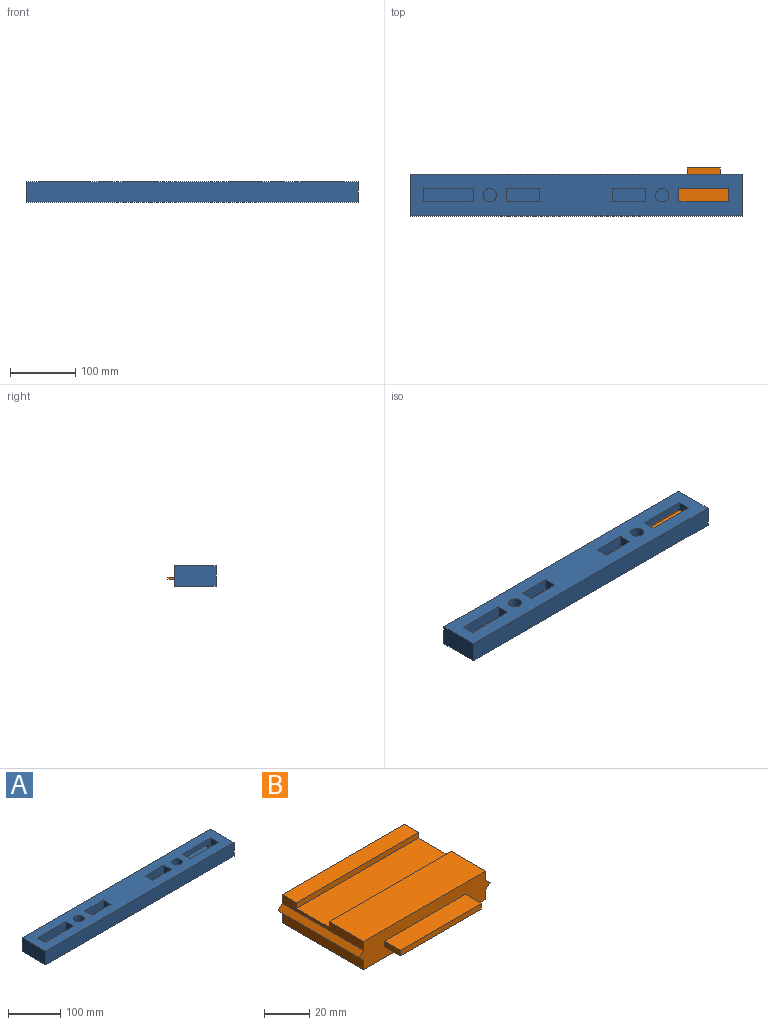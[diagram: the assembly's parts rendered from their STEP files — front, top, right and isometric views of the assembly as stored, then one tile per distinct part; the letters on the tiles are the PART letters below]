
ASSEMBLY  parts=2 mates=1
PART A: 39 faces, bbox 508x63.5x31.8 mm
  f0: plane 508x31.75mm, normal (0,1,0), area 14953.2mm2, adj f3,f4,f6,f7,f13,f14,f29,f30
  f1: plane 76.2x11.43mm, normal (0,-1,0), area 871mm2, adj f3,f13,f14,f29
  f2: plane 76.2x11.43mm, normal (0,1,0), area 871mm2, adj f3,f13,f14,f35
  f3: plane 508x63.5mm, normal (0,0,1), area 26448.1mm2, adj f0,f1,f2,f4,f5,f6,f8,f9
  f4: plane 63.5x31.75mm, normal (-1,0,0), area 2016.1mm2, adj f0,f3,f5,f7
  f5: plane 508x31.75mm, normal (0,-1,0), area 16129mm2, adj f3,f4,f6,f7
  f6: plane 63.5x31.75mm, normal (1,0,0), area 2016.1mm2, adj f0,f3,f5,f7
  f7: plane 508x63.5mm, normal (0,0,-1), area 32258mm2, adj f0,f4,f5,f6
  f8: plane 50.8x18mm, normal (0,-1,0), area 914.4mm2, adj f3,f9,f11,f12
  f9: plane 20.32x18mm, normal (1,0,0), area 365.8mm2, adj f3,f8,f10,f12
  f10: plane 50.8x18mm, normal (0,1,0), area 914.4mm2, adj f3,f9,f11,f12
  f11: plane 20.32x18mm, normal (-1,0,0), area 365.8mm2, adj f3,f8,f10,f12
  f12: plane 50.8x20.32mm, normal (0,0,1), area 1032.3mm2, adj f8,f9,f10,f11
  f13: plane 50.8x16.2mm, normal (1,0,0), area 474.7mm2, adj f0,f1,f2,f3,f29,f34,f35,f38
  f14: plane 50.8x16.2mm, normal (-1,0,0), area 474.7mm2, adj f0,f1,f2,f3,f29,f35,f36,f38
  f15: cylinder r=10.16mm len=20.32mm, axis (0,0,1), area 1149.1mm2, adj f3,f16
  f16: plane 20.32x20.32mm, normal (0,0,1), area 324.3mm2, adj f15
  f17: cylinder r=10.16mm len=20.32mm, axis (0,0,1), area 1149.1mm2, adj f3,f18
  f18: plane 20.32x20.32mm, normal (0,0,1), area 324.3mm2, adj f17
  f19: plane 50.8x18mm, normal (0,1,0), area 914.4mm2, adj f3,f20,f22,f23
  f20: plane 20.32x18mm, normal (-1,0,0), area 365.8mm2, adj f3,f19,f21,f23
  f21: plane 50.8x18mm, normal (0,-1,0), area 914.4mm2, adj f3,f20,f22,f23
  f22: plane 20.32x18mm, normal (1,0,0), area 365.8mm2, adj f3,f19,f21,f23
  f23: plane 50.8x20.32mm, normal (0,0,1), area 1032.3mm2, adj f19,f20,f21,f22
  f24: plane 76.2x18mm, normal (0,-1,0), area 1371.6mm2, adj f3,f25,f27,f28
  f25: plane 20.32x18mm, normal (1,0,0), area 365.8mm2, adj f3,f24,f26,f28
  f26: plane 76.2x18mm, normal (0,1,0), area 1371.6mm2, adj f3,f25,f27,f28
  f27: plane 20.32x18mm, normal (-1,0,0), area 365.8mm2, adj f3,f24,f26,f28
  f28: plane 76.2x20.32mm, normal (0,0,1), area 1548.4mm2, adj f24,f25,f26,f27
  f29: plane 76.2x21.59mm, normal (0,0,-1), area 1645.2mm2, adj f0,f1,f13,f14
  f30: plane 50.8x5.08mm, normal (-1,0,0), area 258.1mm2, adj f0,f31,f37,f38
  f31: plane 76.2x50.8mm, normal (0,0,1), area 3871mm2, adj f0,f30,f32,f38
  f32: plane 50.8x5.08mm, normal (1,0,0), area 258.1mm2, adj f0,f31,f33,f38
  f33: plane 50.8x2.69mm, normal (0.71,0,0.71), area 193.5mm2, adj f0,f32,f34,f38
  f34: plane 50.8x2.69mm, normal (0.71,0,-0.71), area 193.5mm2, adj f0,f13,f33,f38
  f35: plane 76.2x8.89mm, normal (0,0,-1), area 677.4mm2, adj f2,f13,f14,f38
  f36: plane 50.8x2.69mm, normal (-0.71,0,-0.71), area 193.5mm2, adj f0,f14,f37,f38
  f37: plane 50.8x2.69mm, normal (-0.71,0,0.71), area 193.5mm2, adj f0,f30,f36,f38
  f38: plane 81.59x15.24mm, normal (0,1,0), area 1175.8mm2, adj f13,f14,f30,f31,f32,f33,f34,f35
PART B: 21 faces, bbox 81.6x60.8x15.2 mm
  f0: plane 81.59x15.24mm, normal (0,-1,0), area 1023.4mm2, adj f2,f3,f4,f5,f6,f7,f8,f9
  f1: plane 76.2x8.89mm, normal (0,0,1), area 677.4mm2, adj f3,f5,f12,f14
  f2: plane 50.8x2.69mm, normal (0.71,0,0.71), area 193.5mm2, adj f0,f3,f11,f12
  f3: plane 50.8x4.77mm, normal (1,0,0), area 181.4mm2, adj f0,f1,f2,f4,f12,f13,f14,f15
  f4: plane 76.2x21.59mm, normal (0,0,1), area 1645.2mm2, adj f0,f3,f5,f13
  f5: plane 50.8x4.77mm, normal (-1,0,0), area 181.4mm2, adj f0,f1,f4,f6,f12,f13,f14,f15
  f6: plane 50.8x2.69mm, normal (-0.71,0,0.71), area 193.5mm2, adj f0,f5,f7,f12
  f7: plane 50.8x2.69mm, normal (-0.71,0,-0.71), area 193.5mm2, adj f0,f6,f8,f12
  f8: plane 50.8x5.08mm, normal (-1,0,0), area 258.1mm2, adj f0,f7,f9,f12
  f9: plane 76.2x50.8mm, normal (0,0,-1), area 3871mm2, adj f0,f8,f10,f12
  f10: plane 50.8x5.08mm, normal (1,0,0), area 258.1mm2, adj f0,f9,f11,f12
  f11: plane 50.8x2.69mm, normal (0.71,0,-0.71), area 193.5mm2, adj f0,f2,f10,f12
  f12: plane 81.59x15.24mm, normal (0,1,0), area 1175.8mm2, adj f1,f2,f3,f5,f6,f7,f8,f9
  f13: plane 76.2x3mm, normal (0,1,0), area 228.6mm2, adj f3,f4,f5,f15
  f14: plane 76.2x3mm, normal (0,-1,0), area 228.6mm2, adj f1,f3,f5,f15
  f15: plane 76.2x20.32mm, normal (0,0,1), area 1548.4mm2, adj f3,f5,f13,f14
  f16: plane 50.8x10mm, normal (0,0,1), area 508mm2, adj f0,f17,f19,f20
  f17: plane 10x3mm, normal (-1,0,0), area 30mm2, adj f0,f16,f18,f20
  f18: plane 50.8x10mm, normal (0,0,-1), area 508mm2, adj f0,f17,f19,f20
  f19: plane 10x3mm, normal (1,0,0), area 30mm2, adj f0,f16,f18,f20
  f20: plane 50.8x3mm, normal (0,-1,0), area 152.4mm2, adj f16,f17,f18,f19
PLACE A t=(-64.12,-70.84,-66.6)mm
PLACE B rot(axis=(0,0,-1),180deg) t=(131.46,-89.89,-53.9)mm
MATE fastened B.f9 <-> A.f31  axis (0,0,-1) through (131.46,-89.89,-61.52)mm
